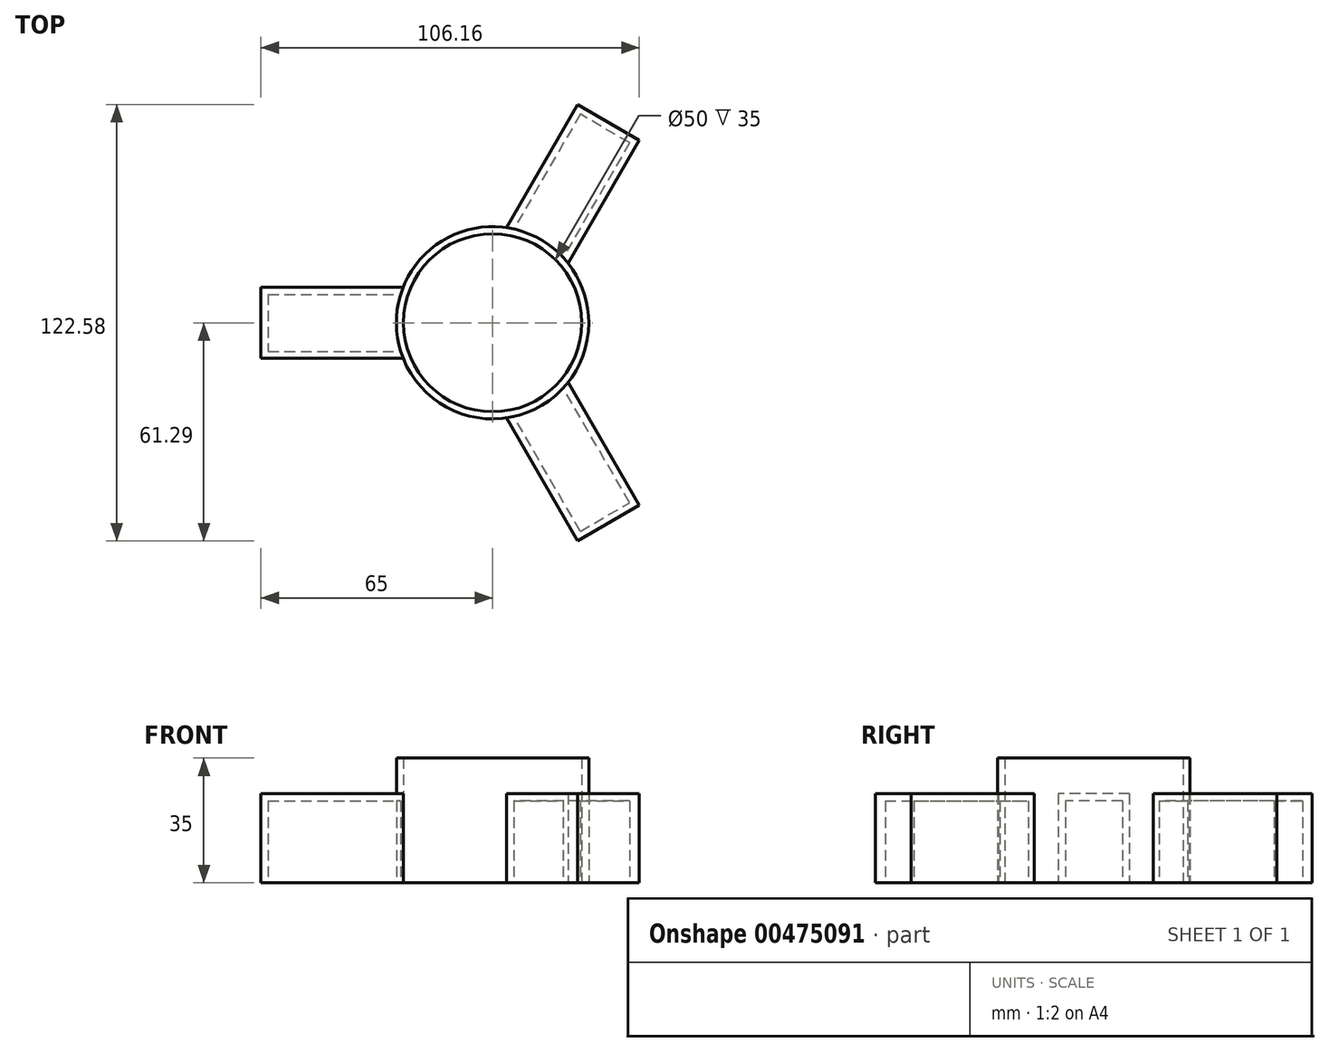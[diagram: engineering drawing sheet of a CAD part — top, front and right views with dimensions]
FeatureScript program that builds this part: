
annotation { "Feature Type Name" : "Feature", "Feature Type Description" : "" }
export const myFeature = defineFeature(function(context is Context, id is Id, definition is map)
    precondition{}
    {
        {
            var Q0;
            Q0=qCreatedBy(makeId("Top.planeOp"),FACE);
            var sketch = newSketch(context, id + "F0", { "sketchPlane" : qUnion([Q0])});
            skCircle(sketch, "E0", {"center": v(0, 0) * mm, "radius": 25 * mm});
            skCircle(sketch, "E1.0", {"center": v(0, 0) * mm, "radius": 27 * mm});
            skLineSegment(sketch, "E2.bottom", {"start": v(-65, 10) * mm, "end": v(-25, 10) * mm});
            skLineSegment(sketch, "E2.top", {"start": v(-65, -10) * mm, "end": v(-25, -10) * mm});
            skLineSegment(sketch, "E2.left", {"start": v(-65, 10) * mm, "end": v(-65, -10) * mm});
            skLineSegment(sketch, "E3.1.0", {"start": v(23.84, -61.3) * mm, "end": v(41.16, -51.3) * mm});
            skLineSegment(sketch, "E3.1.1", {"start": v(23.84, -61.3) * mm, "end": v(3.84, -26.65) * mm});
            skLineSegment(sketch, "E3.1.3", {"start": v(41.16, -51.3) * mm, "end": v(21.16, -16.65) * mm});
            skLineSegment(sketch, "E3.2.0", {"start": v(41.16, 51.3) * mm, "end": v(23.84, 61.3) * mm});
            skLineSegment(sketch, "E3.2.1", {"start": v(41.16, 51.3) * mm, "end": v(21.16, 16.65) * mm});
            skLineSegment(sketch, "E3.2.3", {"start": v(23.84, 61.3) * mm, "end": v(3.84, 26.65) * mm});
            skSolve(sketch);
        }
        {
            var Q0;
            Q0=makeQuery(id+"F0.imprint","IMPRINT",FACE,{"disambiguationData":[TD([[makeQuery(id+"F0.imprint","IMPRINT",EDGE,{"derivedFrom":sQuery(id+"F0.wireOp",EDGE,"E0")}),-1.0]])]});
            extrude(context, id + "F1", {"entities" : qUnion([Q0]), "depth" : 35 * mm});
        }
        {
            var Q0;
            {var subQ0=sQuery(id+"F0.wireOp",EDGE,"E2.left");Q0=makeQuery(id+"F0.imprint","IMPRINT",FACE,{"disambiguationData":[TD([[makeQuery(id+"F0.imprint","IMPRINT",EDGE,{"derivedFrom":subQ0}),1.0]])]});}
            var Q1;
            {var subQ0=sQuery(id+"F0.wireOp",EDGE,"E3.1.0");Q1=makeQuery(id+"F0.imprint","IMPRINT",FACE,{"disambiguationData":[TD([[makeQuery(id+"F0.imprint","IMPRINT",EDGE,{"derivedFrom":subQ0}),1.0]])]});}
            var Q2;
            {var subQ0=sQuery(id+"F0.wireOp",EDGE,"E3.2.0");Q2=makeQuery(id+"F0.imprint","IMPRINT",FACE,{"disambiguationData":[TD([[makeQuery(id+"F0.imprint","IMPRINT",EDGE,{"derivedFrom":subQ0}),1.0]])]});}
            extrude(context, id + "F2", {"entities" : qUnion([Q0, Q1, Q2]), "operationType" : NewBodyOperationType.ADD, "depth" : 25 * mm});
        }
        {
            var Q0;
            {var subQ0=sQuery(id+"F0.wireOp",EDGE,"E1.0");Q0=makeQuery(id+"F2.boolean.opBoolean","MERGE",FACE,{"derivedFrom":[makeQuery(id+"F1.opExtrude","CAP_FACE",FACE,{"disambiguationData":[OSD([sQuery(id+"F0.wireOp",EDGE,"E0"),subQ0])],"isStart":true}),makeQuery(id+"F2.opExtrude","CAP_FACE",FACE,{"disambiguationData":[OSD([sQuery(id+"F0.wireOp",EDGE,"E2.bottom"),sQuery(id+"F0.wireOp",EDGE,"E2.top"),sQuery(id+"F0.wireOp",EDGE,"E2.left"),subQ0])],"isStart":true}),makeQuery(id+"F2.opExtrude","CAP_FACE",FACE,{"disambiguationData":[OSD([sQuery(id+"F0.wireOp",EDGE,"E3.1.0"),sQuery(id+"F0.wireOp",EDGE,"E3.1.1"),sQuery(id+"F0.wireOp",EDGE,"E3.1.3"),subQ0])],"isStart":true}),makeQuery(id+"F2.opExtrude","CAP_FACE",FACE,{"disambiguationData":[OSD([sQuery(id+"F0.wireOp",EDGE,"E3.2.0"),sQuery(id+"F0.wireOp",EDGE,"E3.2.1"),subQ0,sQuery(id+"F0.wireOp",EDGE,"E3.2.3")])],"isStart":true})]});}
            shell(context, id + "F3", {"entities" : qUnion([Q0]), "thickness" : 2 * mm});
        }
    });
